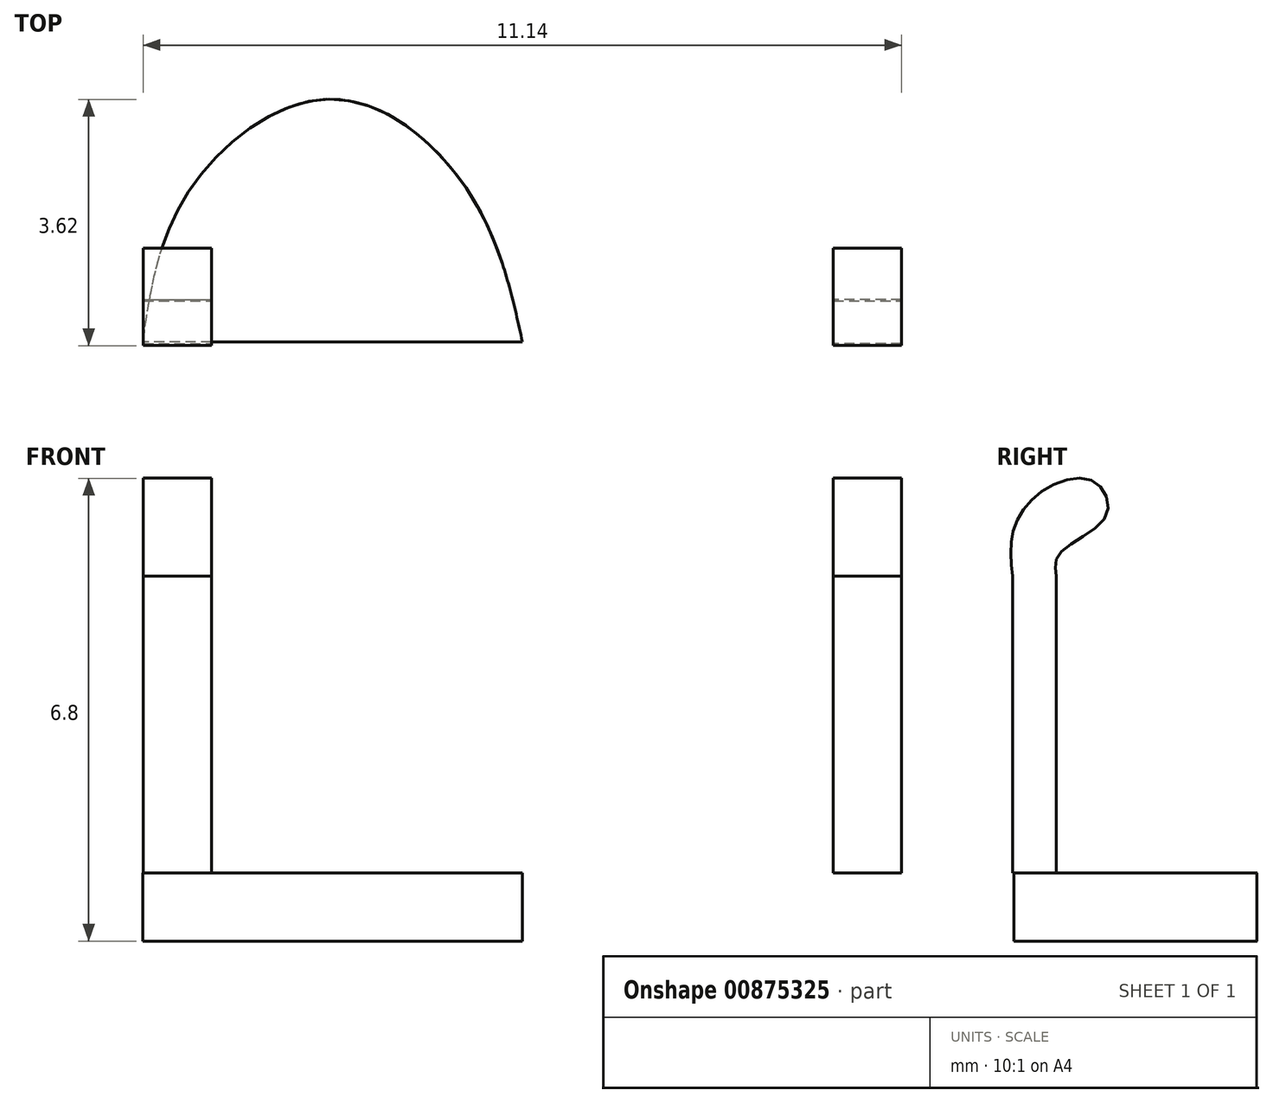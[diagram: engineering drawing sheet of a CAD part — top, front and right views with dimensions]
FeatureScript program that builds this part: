
annotation { "Feature Type Name" : "Feature", "Feature Type Description" : "" }
export const myFeature = defineFeature(function(context is Context, id is Id, definition is map)
    precondition{}
    {
        {
            var Q0;
            Q0=qCreatedBy(makeId("Top.planeOp"),FACE);
            var sketch = newSketch(context, id + "F0", { "sketchPlane" : qUnion([Q0])});
            skLineSegment(sketch, "E0", {"start": v(0, -10.48) * mm, "end": v(5.57, -10.48) * mm});
            skLineSegment(sketch, "E1.MirrorCS", {"start": v(0, -10.48) * mm, "end": v(-5.57, -10.48) * mm});
            skPoint(sketch, "E2", {"position": v(-2.79, -10.48) * mm});
            skPoint(sketch, "E3", {"position": v(-2.79, -6.9) * mm});
            skFitSpline(sketch, "E4", {"points": [v(-5.57, -10.48) * mm, v(-4.85, -8.19) * mm, v(-2.79, -6.9) * mm, v(-0.84, -8.19) * mm, v(0, -10.48) * mm], "startDerivative": vector(1.4, 10.2) * mm, "endDerivative": vector(2.12, -10.11) * mm});
            skPoint(sketch, "E5", {"position": v(2.79, -10.48) * mm});
            skFitSpline(sketch, "E6.MirrorCS", {"points": [v(5.57, -10.48) * mm, v(4.85, -8.19) * mm, v(2.79, -6.9) * mm, v(0.84, -8.19) * mm, v(0, -10.48) * mm], "startDerivative": vector(-1.4, 10.2) * mm, "endDerivative": vector(-2.12, -10.11) * mm});
            skPoint(sketch, "E7", {"position": v(-0.3, -9.33) * mm});
            skPoint(sketch, "E8", {"position": v(0.3, -9.33) * mm});
            skLineSegment(sketch, "E9", {"start": v(-0.3, -9.33) * mm, "end": v(0.3, -9.33) * mm});
            skSolve(sketch);
        }
        {
            var Q0;
            Q0=makeQuery(id+"F0.imprint","IMPRINT",FACE,{"disambiguationData":[TD([[makeQuery(id+"F0.imprint","IMPRINT",EDGE,{"derivedFrom":sQuery(id+"F0.wireOp",EDGE,"E1.MirrorCS")}),-1.0]])]});
            extrude(context, id + "F1", {"entities" : qUnion([Q0]), "oppositeDirection" : true, "depth" : 1 * mm, "offsetDistance" : 25 * mm});
        }
        {
            var Q0;
            Q0=qCreatedBy(makeId("Right.planeOp"),FACE);
            var sketch = newSketch(context, id + "F2", { "sketchPlane" : qUnion([Q0])});
            skLineSegment(sketch, "E10", {"start": v(-9.23, 0) * mm, "end": v(-9.23, 4.36) * mm});
            skLineSegment(sketch, "E11", {"start": v(-8.58, 4.36) * mm, "end": v(-8.58, 0) * mm});
            skPoint(sketch, "E12.5.internal.orphan", {"position": v(-8.58, 4.36) * mm});
            skFitSpline(sketch, "E13", {"points": [v(-9.23, 4.36) * mm, v(-9.23, 5) * mm, v(-8.8, 5.6) * mm, v(-8.04, 5.76) * mm, v(-7.86, 5.25) * mm, v(-8.53, 4.7) * mm, v(-8.58, 4.36) * mm], "startDerivative": vector(-0.45, 3.85) * mm, "endDerivative": vector(0.45, -2.86) * mm});
            skLineSegment(sketch, "E14", {"start": v(-8.58, 0) * mm, "end": v(-9.23, 0) * mm});
            skSolve(sketch);
        }
        {
            var Q0;
            Q0=makeQuery(id+"F2.imprint","IMPRINT",FACE,{"disambiguationData":[TD([[makeQuery(id+"F2.imprint","IMPRINT",EDGE,{"derivedFrom":sQuery(id+"F2.wireOp",EDGE,"E10")}),-1.0]])]});
            var Q1;
            Q1 = qSketchRegion(id + "F6", true);
            extrude(context, id + "F3", {"entities" : qUnion([Q0, Q1]), "depth" : 1 * mm, "offsetDistance" : 25 * mm});
        }
        {
            var Q0;
            Q0=qCreatedBy(makeId("Front.planeOp"),FACE);
            var sketch = newSketch(context, id + "F4", { "sketchPlane" : qUnion([Q0])});
            skLineSegment(sketch, "E15", {"start": v(0, 2.54) * mm, "end": v(5.04, 2.54) * mm});
            skSolve(sketch);
        }
        {
            var Q0;
            Q0=makeQuery(id+"F3.opExtrude","SWEPT_BODY",BODY,{"disambiguationData":[OSD([sQuery(id+"F2.wireOp",EDGE,"E10"),sQuery(id+"F2.wireOp",EDGE,"E11"),sQuery(id+"F2.wireOp",EDGE,"E13"),sQuery(id+"F2.wireOp",EDGE,"E14")])]});
            var Q1;
            Q1=sQuery(id+"F4.wireOp",EDGE,"E15");
            transform(context, id + "F5", {"entities" : qUnion([Q0]), "transformType" : TransformType.TRANSLATION_ENTITY, "oppositeDirectionEntity" : false, "transformLine" : qUnion([Q1]), "makeCopy" : false});
        }
        {
            var Q0;
            Q0=qCreatedBy(makeId("Right.planeOp"),FACE);
            var sketch = newSketch(context, id + "F6", { "sketchPlane" : qUnion([Q0])});
            skLineSegment(sketch, "E16", {"start": v(-8.53, 2.24) * mm, "end": v(-9.8, 2.24) * mm});
            skSolve(sketch);
        }
        {
            var Q0;
            Q0=makeQuery(id+"F3.opExtrude","SWEPT_BODY",BODY,{"disambiguationData":[OSD([sQuery(id+"F2.wireOp",EDGE,"E10"),sQuery(id+"F2.wireOp",EDGE,"E11"),sQuery(id+"F2.wireOp",EDGE,"E13"),sQuery(id+"F2.wireOp",EDGE,"E14")])]});
            var Q1;
            Q1=sQuery(id+"F6.wireOp",EDGE,"E16");
            transform(context, id + "F7", {"entities" : qUnion([Q0]), "transformType" : TransformType.TRANSLATION_ENTITY, "oppositeDirectionEntity" : false, "transformLine" : qUnion([Q1]), "makeCopy" : false});
        }
        {
            var Q0;
            Q0=qCreatedBy(makeId("Front.planeOp"),FACE);
            var sketch = newSketch(context, id + "F8", { "sketchPlane" : qUnion([Q0])});
            skPoint(sketch, "E17", {"position": v(5.38, -0.93) * mm});
            skPoint(sketch, "E18", {"position": v(4.9, -0.93) * mm});
            skLineSegment(sketch, "E19", {"start": v(4.9, -0.93) * mm, "end": v(5.38, -0.93) * mm});
            skSolve(sketch);
        }
        {
            var Q0;
            Q0=makeQuery(id+"F3.opExtrude","SWEPT_BODY",BODY,{"disambiguationData":[OSD([sQuery(id+"F2.wireOp",EDGE,"E10"),sQuery(id+"F2.wireOp",EDGE,"E11"),sQuery(id+"F2.wireOp",EDGE,"E13"),sQuery(id+"F2.wireOp",EDGE,"E14")])]});
            var Q1;
            Q1=sQuery(id+"F8.wireOp",VERTEX,"E17");
            var Q2;
            Q2=sQuery(id+"F8.wireOp",VERTEX,"E18");
            transform(context, id + "F9", {"entities" : qUnion([Q0]), "transformType" : TransformType.TRANSLATION_ENTITY, "oppositeDirectionEntity" : false, "transformLine" : qUnion([Q1, Q2]), "makeCopy" : false});
        }
        {
            var Q0;
            Q0=makeQuery(id+"F3.opExtrude","SWEPT_BODY",BODY,{"disambiguationData":[OSD([sQuery(id+"F2.wireOp",EDGE,"E10"),sQuery(id+"F2.wireOp",EDGE,"E11"),sQuery(id+"F2.wireOp",EDGE,"E13"),sQuery(id+"F2.wireOp",EDGE,"E14")])]});
            var Q1;
            Q1=qCreatedBy(makeId("Right.planeOp"),FACE);
            mirror(context, id + "F10", {"operationType" : NewBodyOperationType.ADD, "entities" : qUnion([Q0]), "mirrorPlane" : qUnion([Q1])});
        }
    });
